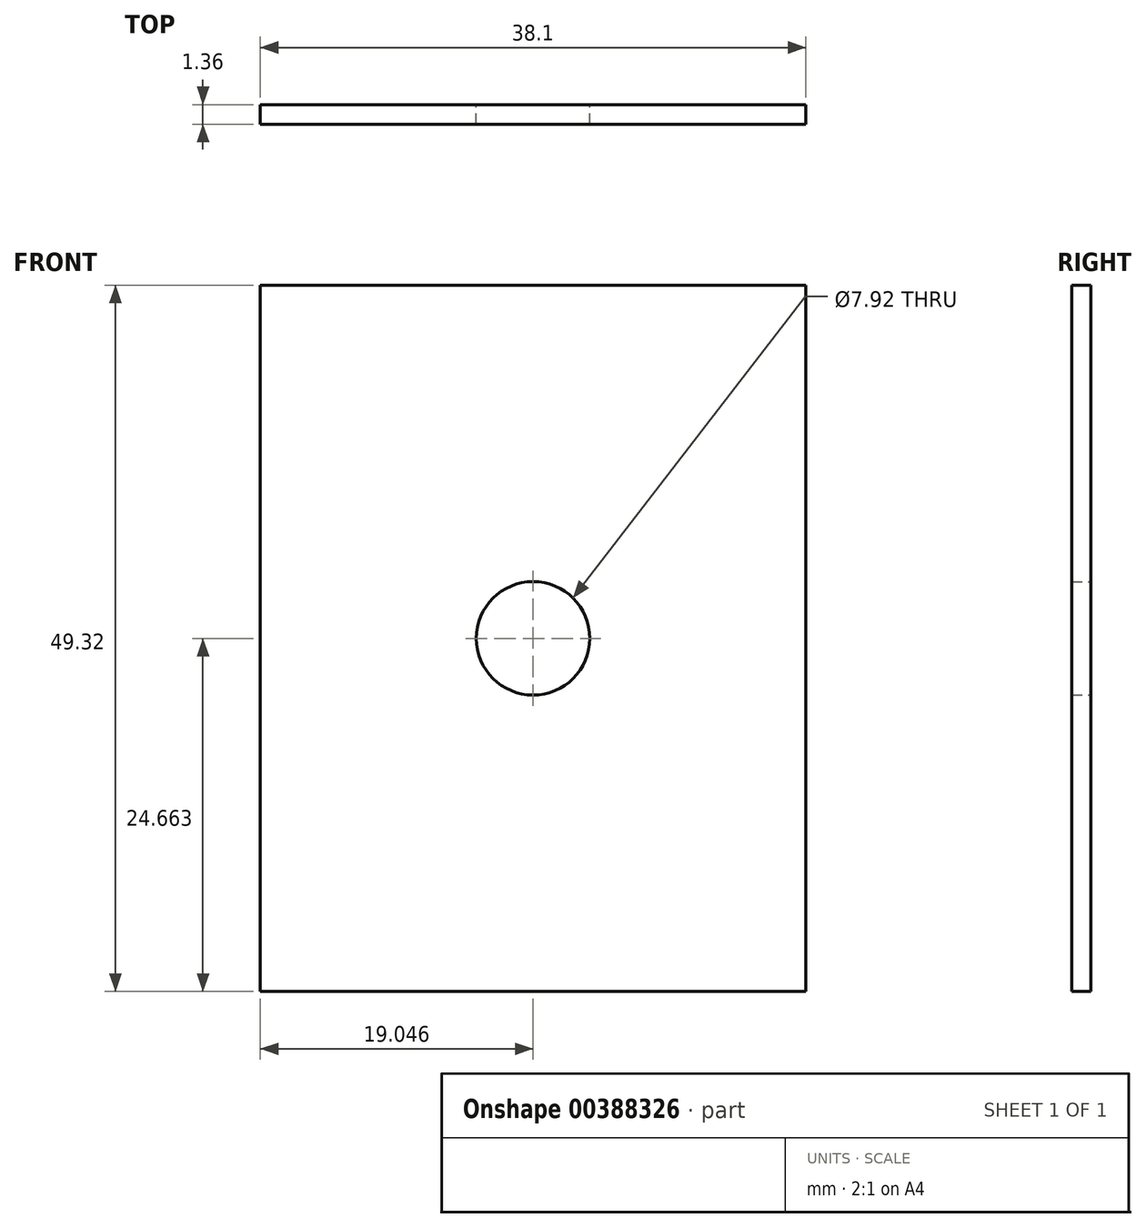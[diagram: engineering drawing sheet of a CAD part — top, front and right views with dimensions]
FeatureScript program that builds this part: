
annotation { "Feature Type Name" : "Feature", "Feature Type Description" : "" }
export const myFeature = defineFeature(function(context is Context, id is Id, definition is map)
    precondition{}
    {
        {
            var Q0;
            Q0=qCreatedBy(makeId("Front.planeOp"),FACE);
            var sketch = newSketch(context, id + "F0", { "sketchPlane" : qUnion([Q0])});
            skLineSegment(sketch, "E0", {"start": v(-26.72, 32.57) * mm, "end": v(11.38, 32.57) * mm});
            skLineSegment(sketch, "E1", {"start": v(11.38, 32.57) * mm, "end": v(11.38, -16.75) * mm});
            skLineSegment(sketch, "E2", {"start": v(11.38, -16.75) * mm, "end": v(-26.72, -16.75) * mm});
            skLineSegment(sketch, "E3", {"start": v(-26.72, -16.75) * mm, "end": v(-26.72, 32.57) * mm});
            skCircle(sketch, "E4", {"center": v(-7.67, 7.91) * mm, "radius": 3.96 * mm});
            skPoint(sketch, "E4.centerSnap0", {"position": v(11.38, 7.91) * mm});
            skPoint(sketch, "E4.centerSnap1", {"position": v(-7.67, 32.57) * mm});
            skSolve(sketch);
        }
        {
            var Q0;
            Q0=makeQuery(id+"F0.imprint","IMPRINT",FACE,{"disambiguationData":[TD([[makeQuery(id+"F0.imprint","IMPRINT",EDGE,{"derivedFrom":sQuery(id+"F0.wireOp",EDGE,"E0")}),-1.0]])]});
            extrude(context, id + "F1", {"entities" : qUnion([Q0]), "depth" : 1.36 * mm});
        }
    });
